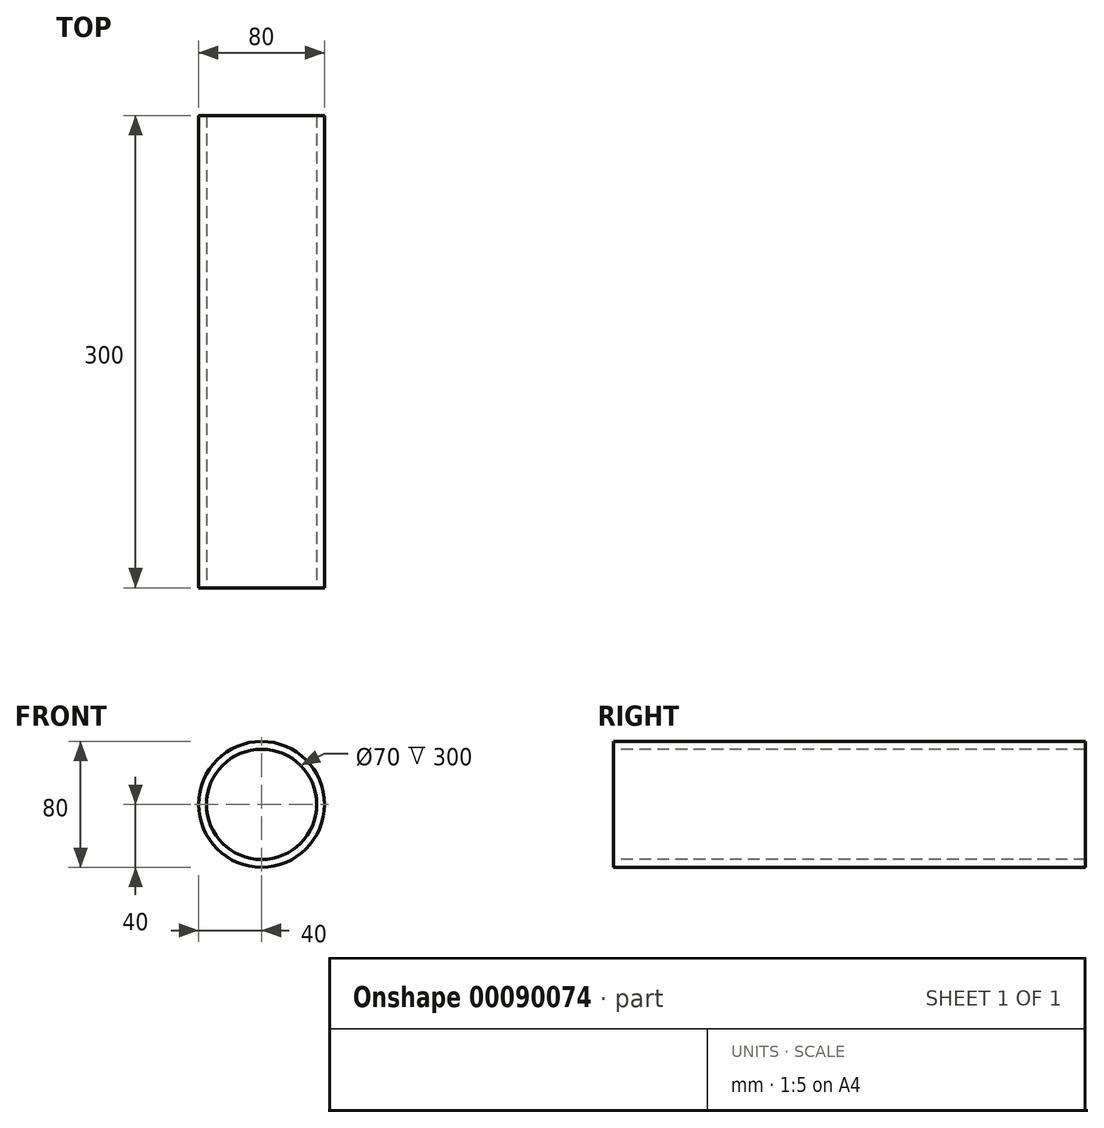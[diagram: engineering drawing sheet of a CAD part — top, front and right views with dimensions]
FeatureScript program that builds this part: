
annotation { "Feature Type Name" : "Feature", "Feature Type Description" : "" }
export const myFeature = defineFeature(function(context is Context, id is Id, definition is map)
    precondition{}
    {
        {
            var Q0;
            Q0=qCreatedBy(makeId("Front.planeOp"),FACE);
            var sketch = newSketch(context, id + "F0", { "sketchPlane" : qUnion([Q0])});
            skCircle(sketch, "E0", {"center": v(0, 0) * mm, "radius": 40 * mm});
            skCircle(sketch, "E1", {"center": v(0, 0) * mm, "radius": 35 * mm});
            skSolve(sketch);
        }
        {
            var Q0;
            Q0=makeQuery(id+"F0.imprint","IMPRINT",FACE,{"disambiguationData":[TD([[makeQuery(id+"F0.imprint","IMPRINT",EDGE,{"derivedFrom":sQuery(id+"F0.wireOp",EDGE,"E0")}),1.0]])]});
            extrude(context, id + "F1", {"entities" : qUnion([Q0]), "oppositeDirection" : true, "depth" : 300 * mm});
        }
    });
